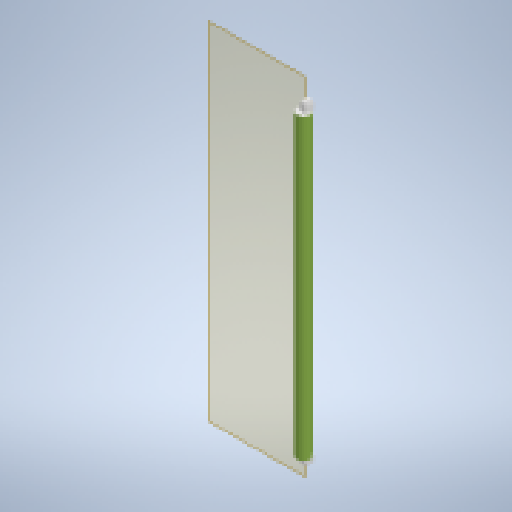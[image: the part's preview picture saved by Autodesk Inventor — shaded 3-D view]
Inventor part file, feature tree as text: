
AUTODESK INVENTOR PART (.ipt)
format: ipt  version: 2023 (Build 270158030, 158C)  size: 177,152 bytes
history: native  units: mm
features: other x3, extrude x2, sketch x2, reference x2, plane x1, fillet x1, projected_geometry x1
ambient origin geometry x8: Origin, YZ Plane, XZ Plane, XY Plane, X Axis, Y Axis, Z Axis, Center Point
bodies: Solid1 (feature_tree), Solid2 (feature_tree)
feature tree (12):
  plane  "Work Plane1"
  extrude  "Extrusion1"  Depth=50.0mm
  fillet  "Fillet1"  Radius=50.0mm
  extrude  "Extrusion2"  Depth=50.0mm TaperAngle=0.0deg
  sketch  "Sketch1"  dims[d0=50.0mm d1=50.0mm d2=50.0mm]
  reference  "Reference1"
  sketch  "Sketch2"  dims[d3=50.0mm d4=50.0mm d5=0.0mm d6=20.0mm d7=25.0mm d8=80.0mm d9=40.0mm d10=50.0mm d11=0.0mm]
  projected_geometry  "Projected Loop1"
  reference  "Reference2"
  other  "primary-engineer-bench.iam"
  other  "bed-base:1"
  other  "bench-end-peice_MIR:1"
